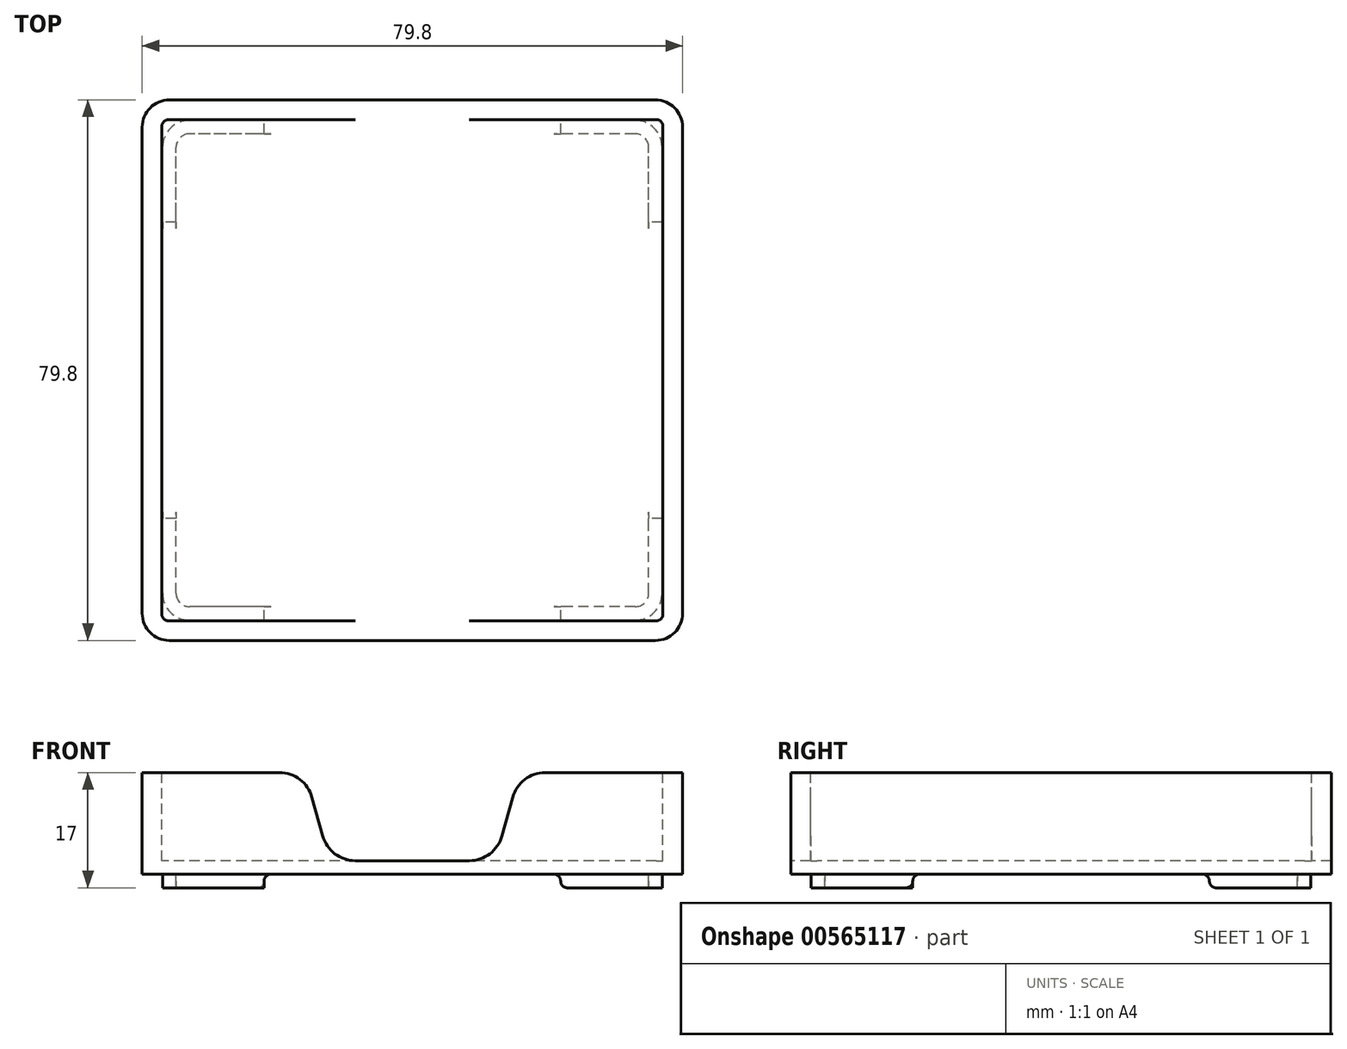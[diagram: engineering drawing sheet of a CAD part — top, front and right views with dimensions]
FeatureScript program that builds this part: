
annotation { "Feature Type Name" : "Feature", "Feature Type Description" : "" }
export const myFeature = defineFeature(function(context is Context, id is Id, definition is map)
    precondition{}
    {
        {
            var Q0;
            Q0=qCreatedBy(makeId("Top.planeOp"),FACE);
            var sketch = newSketch(context, id + "F0", { "sketchPlane" : qUnion([Q0])});
            skLineSegment(sketch, "E0.bottom", {"start": v(39.9, 39.9) * mm, "end": v(-39.9, 39.9) * mm});
            skLineSegment(sketch, "E0.top", {"start": v(39.9, -39.9) * mm, "end": v(-39.9, -39.9) * mm});
            skLineSegment(sketch, "E0.left", {"start": v(39.9, 39.9) * mm, "end": v(39.9, -39.9) * mm});
            skLineSegment(sketch, "E0.right", {"start": v(-39.9, 39.9) * mm, "end": v(-39.9, -39.9) * mm});
            skPoint(sketch, "E0.middle", {"position": v(0, 0) * mm});
            skSolve(sketch);
        }
        {
            var Q0;
            Q0=makeQuery(id+"F0.imprint","IMPRINT",FACE,{"disambiguationData":[TD([[makeQuery(id+"F0.imprint","IMPRINT",EDGE,{"derivedFrom":sQuery(id+"F0.wireOp",EDGE,"E0.bottom")}),1.0]])]});
            extrude(context, id + "F1", {"entities" : qUnion([Q0]), "depth" : 15 * mm, "offsetDistance" : 25 * mm});
        }
        {
            var Q0;
            Q0=makeQuery(id+"F1.opExtrude","CAP_FACE",FACE,{"disambiguationData":[OSD([sQuery(id+"F0.wireOp",EDGE,"E0.bottom"),sQuery(id+"F0.wireOp",EDGE,"E0.top"),sQuery(id+"F0.wireOp",EDGE,"E0.left"),sQuery(id+"F0.wireOp",EDGE,"E0.right")])],"isStart":false});
            var sketch = newSketch(context, id + "F2", { "sketchPlane" : qUnion([Q0])});
            skLineSegment(sketch, "E1.bottom", {"start": v(37, 37) * mm, "end": v(-37, 37) * mm});
            skLineSegment(sketch, "E1.top", {"start": v(37, -37) * mm, "end": v(-37, -37) * mm});
            skLineSegment(sketch, "E1.left", {"start": v(37, 37) * mm, "end": v(37, -37) * mm});
            skLineSegment(sketch, "E1.right", {"start": v(-37, 37) * mm, "end": v(-37, -37) * mm});
            skPoint(sketch, "E1.middle", {"position": v(0, 0) * mm});
            skSolve(sketch);
        }
        {
            var Q0;
            Q0 = qSketchRegion(id + "F2", true);
            extrude(context, id + "F3", {"entities" : qUnion([Q0]), "operationType" : NewBodyOperationType.REMOVE, "oppositeDirection" : true, "depth" : 13 * mm, "offsetDistance" : 25 * mm});
        }
        {
            var Q0;
            Q0=makeQuery(id+"F1.opExtrude","CAP_FACE",FACE,{"disambiguationData":[OSD([sQuery(id+"F0.wireOp",EDGE,"E0.bottom"),sQuery(id+"F0.wireOp",EDGE,"E0.top"),sQuery(id+"F0.wireOp",EDGE,"E0.left"),sQuery(id+"F0.wireOp",EDGE,"E0.right")])],"isStart":true});
            var sketch = newSketch(context, id + "F4", { "sketchPlane" : qUnion([Q0])});
            skLineSegment(sketch, "E2.bottom", {"start": v(36.9, 36.9) * mm, "end": v(-36.9, 36.9) * mm});
            skLineSegment(sketch, "E2.top", {"start": v(36.9, -36.9) * mm, "end": v(-36.9, -36.9) * mm});
            skLineSegment(sketch, "E2.left", {"start": v(36.9, 36.9) * mm, "end": v(36.9, -36.9) * mm});
            skLineSegment(sketch, "E2.right", {"start": v(-36.9, 36.9) * mm, "end": v(-36.9, -36.9) * mm});
            skPoint(sketch, "E2.middle", {"position": v(0, 0) * mm});
            skLineSegment(sketch, "E3.bottom", {"start": v(34.9, 34.9) * mm, "end": v(-34.9, 34.9) * mm});
            skLineSegment(sketch, "E3.top", {"start": v(34.9, -34.9) * mm, "end": v(-34.9, -34.9) * mm});
            skLineSegment(sketch, "E3.left", {"start": v(34.9, 34.9) * mm, "end": v(34.9, -34.9) * mm});
            skLineSegment(sketch, "E3.right", {"start": v(-34.9, 34.9) * mm, "end": v(-34.9, -34.9) * mm});
            skSolve(sketch);
        }
        {
            var Q0;
            Q0 = qSketchRegion(id + "F4", true);
            extrude(context, id + "F5", {"entities" : qUnion([Q0]), "operationType" : NewBodyOperationType.ADD, "depth" : 2 * mm, "offsetDistance" : 25 * mm});
        }
        {
            var Q0;
            Q0=makeQuery(id+"F5.opExtrude","CAP_FACE",FACE,{"disambiguationData":[OSD([sQuery(id+"F4.wireOp",EDGE,"E2.bottom"),sQuery(id+"F4.wireOp",EDGE,"E2.top"),sQuery(id+"F4.wireOp",EDGE,"E2.left"),sQuery(id+"F4.wireOp",EDGE,"E2.right"),sQuery(id+"F4.wireOp",EDGE,"E3.bottom"),sQuery(id+"F4.wireOp",EDGE,"E3.top"),sQuery(id+"F4.wireOp",EDGE,"E3.left"),sQuery(id+"F4.wireOp",EDGE,"E3.right")])],"isStart":false});
            var sketch = newSketch(context, id + "F6", { "sketchPlane" : qUnion([Q0])});
            skLineSegment(sketch, "E4.bottom", {"start": v(36.9, 21.9) * mm, "end": v(21.9, 21.9) * mm});
            skLineSegment(sketch, "E4.top", {"start": v(36.9, -21.9) * mm, "end": v(21.9, -21.9) * mm});
            skLineSegment(sketch, "E4.left", {"start": v(36.9, 21.9) * mm, "end": v(36.9, -21.9) * mm});
            skLineSegment(sketch, "E4.right", {"start": v(-36.9, 21.9) * mm, "end": v(-36.9, -21.9) * mm});
            skPoint(sketch, "E4.middle", {"position": v(0, 0) * mm});
            skLineSegment(sketch, "E5.bottom", {"start": v(-21.9, 36.9) * mm, "end": v(21.9, 36.9) * mm});
            skLineSegment(sketch, "E5.top", {"start": v(-21.9, -36.9) * mm, "end": v(21.9, -36.9) * mm});
            skLineSegment(sketch, "E5.left", {"start": v(-21.9, 36.9) * mm, "end": v(-21.9, 21.9) * mm});
            skLineSegment(sketch, "E5.right", {"start": v(21.9, 36.9) * mm, "end": v(21.9, 21.9) * mm});
            skLineSegment(sketch, "E6.trimOffspring", {"start": v(-21.9, -21.9) * mm, "end": v(-21.9, -36.9) * mm});
            skLineSegment(sketch, "E7.trimOffspring", {"start": v(-21.9, 21.9) * mm, "end": v(-36.9, 21.9) * mm});
            skLineSegment(sketch, "E8.trimOffspring", {"start": v(21.9, -21.9) * mm, "end": v(21.9, -36.9) * mm});
            skLineSegment(sketch, "E9.trimOffspring", {"start": v(-21.9, -21.9) * mm, "end": v(-36.9, -21.9) * mm});
            skSolve(sketch);
        }
        {
            var Q0;
            Q0 = qSketchRegion(id + "F6", true);
            var Q1;
            Q1=makeQuery(id+"F5.boolean.opBoolean","SPLIT",FACE,{"disambiguationData":[TD([makeQuery(id+"F5.opExtrude","SWEPT_FACE",FACE,{"disambiguationData":[OSD([sQuery(id+"F4.wireOp",EDGE,"E3.bottom")])]})])],"derivedFrom":makeQuery(id+"F1.opExtrude","CAP_FACE",FACE,{"disambiguationData":[OSD([sQuery(id+"F0.wireOp",EDGE,"E0.bottom"),sQuery(id+"F0.wireOp",EDGE,"E0.top"),sQuery(id+"F0.wireOp",EDGE,"E0.left"),sQuery(id+"F0.wireOp",EDGE,"E0.right")])],"isStart":true})});
            extrude(context, id + "F7", {"entities" : qUnion([Q0]), "operationType" : NewBodyOperationType.REMOVE, "endBound" : BoundingType.UP_TO_SURFACE, "oppositeDirection" : true, "depth" : 25 * mm, "endBoundEntityFace" : qUnion([Q1]), "offsetDistance" : 25 * mm});
        }
        {
            var Q0;
            Q0=makeQuery(id+"F5.opExtrude","SWEPT_EDGE",EDGE,{"disambiguationData":[OSD([sQuery(id+"F4.wireOp",EDGE,"E3.top"),sQuery(id+"F4.wireOp",EDGE,"E3.right")])]});
            var Q1;
            Q1=makeQuery(id+"F5.opExtrude","SWEPT_EDGE",EDGE,{"disambiguationData":[OSD([sQuery(id+"F4.wireOp",EDGE,"E3.bottom"),sQuery(id+"F4.wireOp",EDGE,"E3.right")])]});
            var Q2;
            Q2=makeQuery(id+"F5.opExtrude","SWEPT_EDGE",EDGE,{"disambiguationData":[OSD([sQuery(id+"F4.wireOp",EDGE,"E3.bottom"),sQuery(id+"F4.wireOp",EDGE,"E3.left")])]});
            var Q3;
            Q3=makeQuery(id+"F5.opExtrude","SWEPT_EDGE",EDGE,{"disambiguationData":[OSD([sQuery(id+"F4.wireOp",EDGE,"E3.top"),sQuery(id+"F4.wireOp",EDGE,"E3.left")])]});
            fillet(context, id + "F8", {"entities" : qUnion([Q0, Q1, Q2, Q3]), "radius" : 2 * mm, "tangentPropagation" : true, "allowEdgeOverflow" : false});
        }
        {
            var Q0;
            Q0=makeQuery(id+"F5.opExtrude","SWEPT_EDGE",EDGE,{"disambiguationData":[OSD([sQuery(id+"F4.wireOp",EDGE,"E2.top"),sQuery(id+"F4.wireOp",EDGE,"E2.right")])]});
            var Q1;
            Q1=makeQuery(id+"F5.opExtrude","SWEPT_EDGE",EDGE,{"disambiguationData":[OSD([sQuery(id+"F4.wireOp",EDGE,"E2.top"),sQuery(id+"F4.wireOp",EDGE,"E2.left")])]});
            var Q2;
            Q2=makeQuery(id+"F5.opExtrude","SWEPT_EDGE",EDGE,{"disambiguationData":[OSD([sQuery(id+"F4.wireOp",EDGE,"E2.bottom"),sQuery(id+"F4.wireOp",EDGE,"E2.left")])]});
            var Q3;
            Q3=makeQuery(id+"F5.opExtrude","SWEPT_EDGE",EDGE,{"disambiguationData":[OSD([sQuery(id+"F4.wireOp",EDGE,"E2.bottom"),sQuery(id+"F4.wireOp",EDGE,"E2.right")])]});
            fillet(context, id + "F9", {"entities" : qUnion([Q0, Q1, Q2, Q3]), "radius" : 4 * mm, "tangentPropagation" : true, "allowEdgeOverflow" : false});
        }
        {
            var Q0;
            Q0=makeQuery(id+"F7.boolean.opBoolean","COPY",EDGE,{"derivedFrom":makeQuery(id+"F7.opExtrude","CAP_EDGE",EDGE,{"disambiguationData":[OSD([sQuery(id+"F6.wireOp",EDGE,"E5.right")])],"isStart":true})});
            var Q1;
            Q1=makeQuery(id+"F7.boolean.opBoolean","COPY",EDGE,{"derivedFrom":makeQuery(id+"F7.opExtrude","CAP_EDGE",EDGE,{"disambiguationData":[OSD([sQuery(id+"F6.wireOp",EDGE,"E5.right")])],"isStart":false})});
            var Q2;
            Q2=makeQuery(id+"F7.boolean.opBoolean","COPY",EDGE,{"derivedFrom":makeQuery(id+"F7.opExtrude","CAP_EDGE",EDGE,{"disambiguationData":[OSD([sQuery(id+"F6.wireOp",EDGE,"E4.bottom")])],"isStart":true})});
            var Q3;
            Q3=makeQuery(id+"F7.boolean.opBoolean","COPY",EDGE,{"derivedFrom":makeQuery(id+"F7.opExtrude","CAP_EDGE",EDGE,{"disambiguationData":[OSD([sQuery(id+"F6.wireOp",EDGE,"E4.bottom")])],"isStart":false})});
            var Q4;
            Q4=makeQuery(id+"F7.boolean.opBoolean","COPY",EDGE,{"derivedFrom":makeQuery(id+"F7.opExtrude","CAP_EDGE",EDGE,{"disambiguationData":[OSD([sQuery(id+"F6.wireOp",EDGE,"E7.trimOffspring")])],"isStart":true})});
            var Q5;
            Q5=makeQuery(id+"F7.boolean.opBoolean","COPY",EDGE,{"derivedFrom":makeQuery(id+"F7.opExtrude","CAP_EDGE",EDGE,{"disambiguationData":[OSD([sQuery(id+"F6.wireOp",EDGE,"E7.trimOffspring")])],"isStart":false})});
            var Q6;
            Q6=makeQuery(id+"F7.boolean.opBoolean","COPY",EDGE,{"derivedFrom":makeQuery(id+"F7.opExtrude","CAP_EDGE",EDGE,{"disambiguationData":[OSD([sQuery(id+"F6.wireOp",EDGE,"E5.left")])],"isStart":true})});
            var Q7;
            Q7=makeQuery(id+"F7.boolean.opBoolean","COPY",EDGE,{"derivedFrom":makeQuery(id+"F7.opExtrude","CAP_EDGE",EDGE,{"disambiguationData":[OSD([sQuery(id+"F6.wireOp",EDGE,"E5.left")])],"isStart":false})});
            var Q8;
            Q8=makeQuery(id+"F7.boolean.opBoolean","COPY",EDGE,{"derivedFrom":makeQuery(id+"F7.opExtrude","CAP_EDGE",EDGE,{"disambiguationData":[OSD([sQuery(id+"F6.wireOp",EDGE,"E9.trimOffspring")])],"isStart":true})});
            var Q9;
            Q9=makeQuery(id+"F7.boolean.opBoolean","COPY",EDGE,{"derivedFrom":makeQuery(id+"F7.opExtrude","CAP_EDGE",EDGE,{"disambiguationData":[OSD([sQuery(id+"F6.wireOp",EDGE,"E9.trimOffspring")])],"isStart":false})});
            var Q10;
            Q10=makeQuery(id+"F7.boolean.opBoolean","COPY",EDGE,{"derivedFrom":makeQuery(id+"F7.opExtrude","CAP_EDGE",EDGE,{"disambiguationData":[OSD([sQuery(id+"F6.wireOp",EDGE,"E6.trimOffspring")])],"isStart":true})});
            var Q11;
            Q11=makeQuery(id+"F7.boolean.opBoolean","COPY",EDGE,{"derivedFrom":makeQuery(id+"F7.opExtrude","CAP_EDGE",EDGE,{"disambiguationData":[OSD([sQuery(id+"F6.wireOp",EDGE,"E6.trimOffspring")])],"isStart":false})});
            var Q12;
            Q12=makeQuery(id+"F7.boolean.opBoolean","COPY",EDGE,{"derivedFrom":makeQuery(id+"F7.opExtrude","CAP_EDGE",EDGE,{"disambiguationData":[OSD([sQuery(id+"F6.wireOp",EDGE,"E8.trimOffspring")])],"isStart":true})});
            var Q13;
            Q13=makeQuery(id+"F7.boolean.opBoolean","COPY",EDGE,{"derivedFrom":makeQuery(id+"F7.opExtrude","CAP_EDGE",EDGE,{"disambiguationData":[OSD([sQuery(id+"F6.wireOp",EDGE,"E8.trimOffspring")])],"isStart":false})});
            var Q14;
            Q14=makeQuery(id+"F7.boolean.opBoolean","COPY",EDGE,{"derivedFrom":makeQuery(id+"F7.opExtrude","CAP_EDGE",EDGE,{"disambiguationData":[OSD([sQuery(id+"F6.wireOp",EDGE,"E4.top")])],"isStart":true})});
            var Q15;
            Q15=makeQuery(id+"F7.boolean.opBoolean","COPY",EDGE,{"derivedFrom":makeQuery(id+"F7.opExtrude","CAP_EDGE",EDGE,{"disambiguationData":[OSD([sQuery(id+"F6.wireOp",EDGE,"E4.top")])],"isStart":false})});
            var Q16;
            Q16=makeQuery(id+"F7.boolean.opBoolean","COPY",EDGE,{"derivedFrom":makeQuery(id+"F7.opExtrude","CAP_EDGE",EDGE,{"disambiguationData":[OSD([sQuery(id+"F6.wireOp",EDGE,"E4.top")])],"isStart":false})});
            fillet(context, id + "F10", {"entities" : qUnion([Q0, Q1, Q2, Q3, Q4, Q5, Q6, Q7, Q8, Q9, Q10, Q11, Q12, Q13, Q14, Q15, Q16]), "radius" : 1 * mm, "tangentPropagation" : true, "allowEdgeOverflow" : false});
        }
        {
            var Q0;
            Q0=makeQuery(id+"F1.opExtrude","SWEPT_FACE",FACE,{"disambiguationData":[OSD([sQuery(id+"F0.wireOp",EDGE,"E0.top")])]});
            var sketch = newSketch(context, id + "F11", { "sketchPlane" : qUnion([Q0])});
            skLineSegment(sketch, "E10", {"start": v(-22.33, 30) * mm, "end": v(44.47, 30) * mm, "construction": true});
            skLineSegment(sketch, "E11", {"start": v(-15.04, -15) * mm, "end": v(49.84, -15) * mm, "construction": true});
            skLineSegment(sketch, "E12", {"start": v(-20, 30) * mm, "end": v(-12.22, 2) * mm});
            skLineSegment(sketch, "E13", {"start": v(20, 30) * mm, "end": v(12.22, 2) * mm});
            skLineSegment(sketch, "E14", {"start": v(-12.22, 2) * mm, "end": v(12.22, 2) * mm});
            skLineSegment(sketch, "E15", {"start": v(-20, 30) * mm, "end": v(20, 30) * mm});
            skLineSegment(sketch, "E16", {"start": v(-12.22, 2) * mm, "end": v(-7.5, -15) * mm, "construction": true});
            skLineSegment(sketch, "E17", {"start": v(12.22, 2) * mm, "end": v(7.5, -15) * mm, "construction": true});
            skSolve(sketch);
        }
        {
            var Q0;
            Q0 = qSketchRegion(id + "F11", true);
            extrude(context, id + "F12", {"entities" : qUnion([Q0]), "operationType" : NewBodyOperationType.REMOVE, "endBound" : BoundingType.THROUGH_ALL, "oppositeDirection" : true, "depth" : 25 * mm, "offsetDistance" : 25 * mm});
        }
        {
            var Q0;
            Q0=makeQuery(id+"F12.boolean.opBoolean","INTERSECT",EDGE,{"disambiguationData":[OD(1.0)],"derivedFrom":[makeQuery(id+"F1.opExtrude","CAP_FACE",FACE,{"disambiguationData":[OSD([sQuery(id+"F0.wireOp",EDGE,"E0.bottom"),sQuery(id+"F0.wireOp",EDGE,"E0.top"),sQuery(id+"F0.wireOp",EDGE,"E0.left"),sQuery(id+"F0.wireOp",EDGE,"E0.right")])],"isStart":false}),makeQuery(id+"F12.opExtrude","SWEPT_FACE",FACE,{"disambiguationData":[OSD([sQuery(id+"F11.wireOp",EDGE,"E12")])]})]});
            var Q1;
            Q1=makeQuery(id+"F12.boolean.opBoolean","INTERSECT",EDGE,{"disambiguationData":[OD(1.0)],"derivedFrom":[makeQuery(id+"F1.opExtrude","CAP_FACE",FACE,{"disambiguationData":[OSD([sQuery(id+"F0.wireOp",EDGE,"E0.bottom"),sQuery(id+"F0.wireOp",EDGE,"E0.top"),sQuery(id+"F0.wireOp",EDGE,"E0.left"),sQuery(id+"F0.wireOp",EDGE,"E0.right")])],"isStart":false}),makeQuery(id+"F12.opExtrude","SWEPT_FACE",FACE,{"disambiguationData":[OSD([sQuery(id+"F11.wireOp",EDGE,"E13")])]})]});
            var Q2;
            {var subQ0=sQuery(id+"F11.wireOp",EDGE,"E12");var subQ2=sQuery(id+"F11.wireOp",EDGE,"E14");Q2=makeQuery(id+"F12.boolean.opBoolean","COPY",EDGE,{"disambiguationData":[TD([makeQuery(id+"F1.opExtrude","SWEPT_FACE",FACE,{"disambiguationData":[OSD([sQuery(id+"F0.wireOp",EDGE,"E0.bottom")])]})])],"derivedFrom":makeQuery(id+"F12.opExtrude","SWEPT_EDGE",EDGE,{"disambiguationData":[OSD([subQ0,subQ2])]})});}
            var Q3;
            Q3=makeQuery(id+"F12.boolean.opBoolean","INTERSECT",EDGE,{"disambiguationData":[OD(0.0)],"derivedFrom":[makeQuery(id+"F1.opExtrude","CAP_FACE",FACE,{"disambiguationData":[OSD([sQuery(id+"F0.wireOp",EDGE,"E0.bottom"),sQuery(id+"F0.wireOp",EDGE,"E0.top"),sQuery(id+"F0.wireOp",EDGE,"E0.left"),sQuery(id+"F0.wireOp",EDGE,"E0.right")])],"isStart":false}),makeQuery(id+"F12.opExtrude","SWEPT_FACE",FACE,{"disambiguationData":[OSD([sQuery(id+"F11.wireOp",EDGE,"E12")])]})]});
            var Q4;
            {var subQ1=sQuery(id+"F11.wireOp",EDGE,"E12");var subQ2=sQuery(id+"F11.wireOp",EDGE,"E14");Q4=makeQuery(id+"F12.boolean.opBoolean","COPY",EDGE,{"disambiguationData":[TD([makeQuery(id+"F1.opExtrude","SWEPT_FACE",FACE,{"disambiguationData":[OSD([sQuery(id+"F0.wireOp",EDGE,"E0.top")])]})])],"derivedFrom":makeQuery(id+"F12.opExtrude","SWEPT_EDGE",EDGE,{"disambiguationData":[OSD([subQ1,subQ2])]})});}
            var Q5;
            {var subQ0=sQuery(id+"F11.wireOp",EDGE,"E13");var subQ2=sQuery(id+"F11.wireOp",EDGE,"E14");Q5=makeQuery(id+"F12.boolean.opBoolean","COPY",EDGE,{"disambiguationData":[TD([makeQuery(id+"F1.opExtrude","SWEPT_FACE",FACE,{"disambiguationData":[OSD([sQuery(id+"F0.wireOp",EDGE,"E0.top")])]})])],"derivedFrom":makeQuery(id+"F12.opExtrude","SWEPT_EDGE",EDGE,{"disambiguationData":[OSD([subQ0,subQ2])]})});}
            var Q6;
            Q6=makeQuery(id+"F12.boolean.opBoolean","INTERSECT",EDGE,{"disambiguationData":[OD(0.0)],"derivedFrom":[makeQuery(id+"F1.opExtrude","CAP_FACE",FACE,{"disambiguationData":[OSD([sQuery(id+"F0.wireOp",EDGE,"E0.bottom"),sQuery(id+"F0.wireOp",EDGE,"E0.top"),sQuery(id+"F0.wireOp",EDGE,"E0.left"),sQuery(id+"F0.wireOp",EDGE,"E0.right")])],"isStart":false}),makeQuery(id+"F12.opExtrude","SWEPT_FACE",FACE,{"disambiguationData":[OSD([sQuery(id+"F11.wireOp",EDGE,"E13")])]})]});
            var Q7;
            {var subQ0=sQuery(id+"F11.wireOp",EDGE,"E13");var subQ2=sQuery(id+"F11.wireOp",EDGE,"E14");Q7=makeQuery(id+"F12.boolean.opBoolean","COPY",EDGE,{"disambiguationData":[TD([makeQuery(id+"F1.opExtrude","SWEPT_FACE",FACE,{"disambiguationData":[OSD([sQuery(id+"F0.wireOp",EDGE,"E0.bottom")])]})])],"derivedFrom":makeQuery(id+"F12.opExtrude","SWEPT_EDGE",EDGE,{"disambiguationData":[OSD([subQ0,subQ2])]})});}
            fillet(context, id + "F13", {"entities" : qUnion([Q0, Q1, Q2, Q3, Q4, Q5, Q6, Q7]), "radius" : 5 * mm, "tangentPropagation" : true, "allowEdgeOverflow" : false});
        }
        {
            var Q0;
            Q0=makeQuery(id+"F1.opExtrude","SWEPT_EDGE",EDGE,{"disambiguationData":[OSD([sQuery(id+"F0.wireOp",EDGE,"E0.top"),sQuery(id+"F0.wireOp",EDGE,"E0.left")])]});
            var Q1;
            Q1=makeQuery(id+"F1.opExtrude","SWEPT_EDGE",EDGE,{"disambiguationData":[OSD([sQuery(id+"F0.wireOp",EDGE,"E0.bottom"),sQuery(id+"F0.wireOp",EDGE,"E0.left")])]});
            var Q2;
            Q2=makeQuery(id+"F1.opExtrude","SWEPT_EDGE",EDGE,{"disambiguationData":[OSD([sQuery(id+"F0.wireOp",EDGE,"E0.top"),sQuery(id+"F0.wireOp",EDGE,"E0.right")])]});
            var Q3;
            Q3=makeQuery(id+"F1.opExtrude","SWEPT_EDGE",EDGE,{"disambiguationData":[OSD([sQuery(id+"F0.wireOp",EDGE,"E0.bottom"),sQuery(id+"F0.wireOp",EDGE,"E0.right")])]});
            fillet(context, id + "F14", {"entities" : qUnion([Q0, Q1, Q2, Q3]), "radius" : 4 * mm, "tangentPropagation" : true, "allowEdgeOverflow" : false});
        }
        {
            var Q0;
            Q0=makeQuery(id+"F3.boolean.opBoolean","COPY",EDGE,{"derivedFrom":makeQuery(id+"F3.opExtrude","SWEPT_EDGE",EDGE,{"disambiguationData":[OSD([sQuery(id+"F2.wireOp",EDGE,"E1.bottom"),sQuery(id+"F2.wireOp",EDGE,"E1.left")])]})});
            var Q1;
            Q1=makeQuery(id+"F3.boolean.opBoolean","COPY",EDGE,{"derivedFrom":makeQuery(id+"F3.opExtrude","SWEPT_EDGE",EDGE,{"disambiguationData":[OSD([sQuery(id+"F2.wireOp",EDGE,"E1.bottom"),sQuery(id+"F2.wireOp",EDGE,"E1.right")])]})});
            var Q2;
            Q2=makeQuery(id+"F3.boolean.opBoolean","COPY",EDGE,{"derivedFrom":makeQuery(id+"F3.opExtrude","SWEPT_EDGE",EDGE,{"disambiguationData":[OSD([sQuery(id+"F2.wireOp",EDGE,"E1.top"),sQuery(id+"F2.wireOp",EDGE,"E1.right")])]})});
            var Q3;
            Q3=makeQuery(id+"F3.boolean.opBoolean","COPY",EDGE,{"derivedFrom":makeQuery(id+"F3.opExtrude","SWEPT_EDGE",EDGE,{"disambiguationData":[OSD([sQuery(id+"F2.wireOp",EDGE,"E1.top"),sQuery(id+"F2.wireOp",EDGE,"E1.left")])]})});
            fillet(context, id + "F15", {"entities" : qUnion([Q0, Q1, Q2, Q3]), "radius" : 1 * mm, "tangentPropagation" : true, "allowEdgeOverflow" : false});
        }
    });
